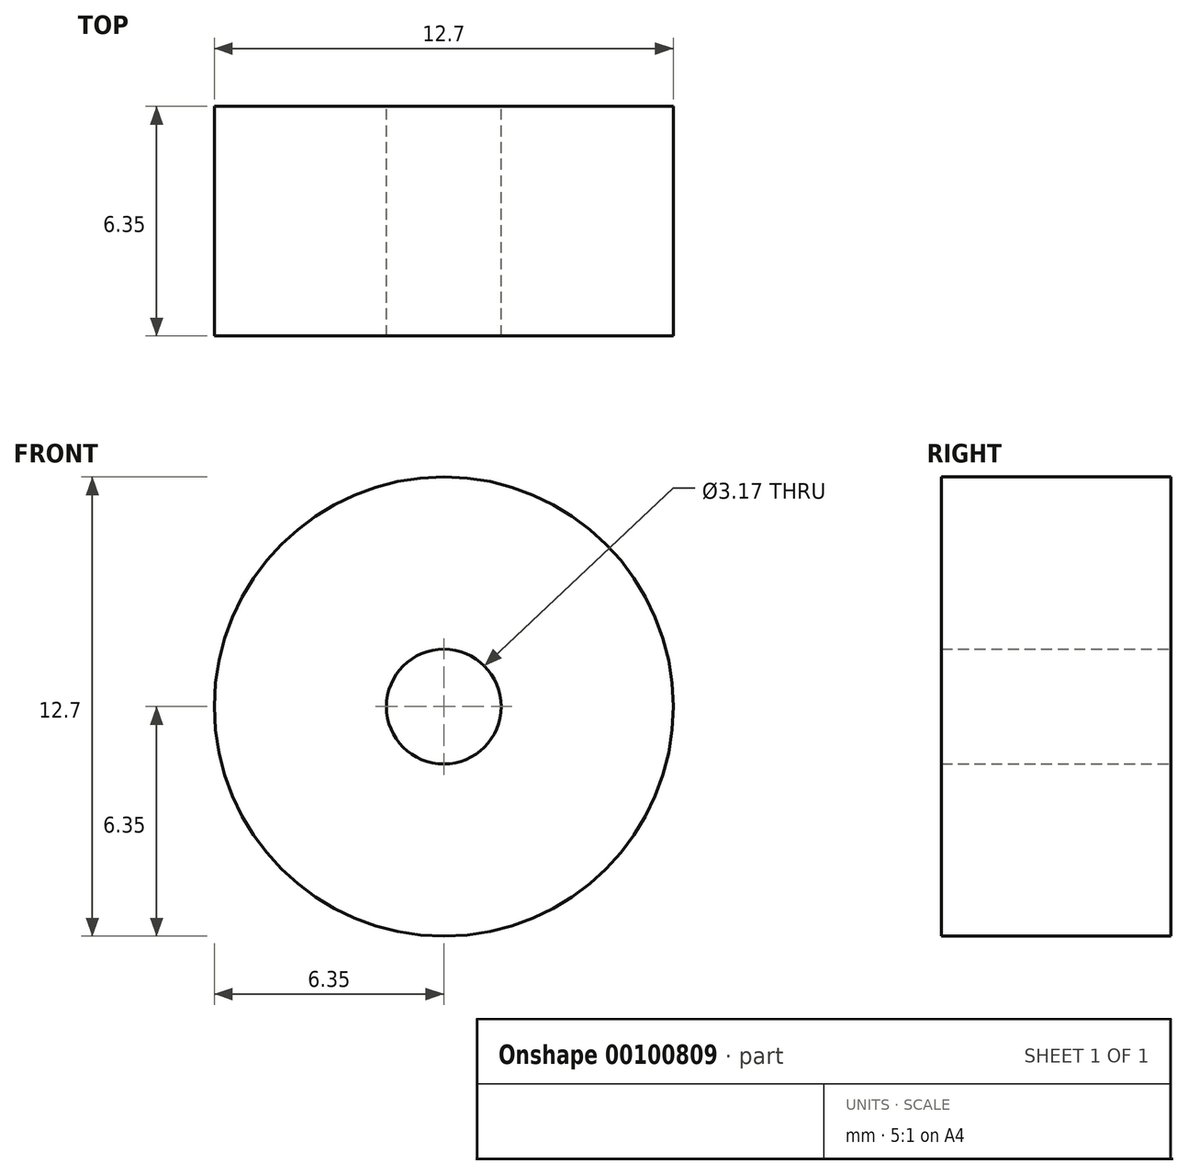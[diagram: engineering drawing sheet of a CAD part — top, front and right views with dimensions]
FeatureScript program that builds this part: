
annotation { "Feature Type Name" : "Feature", "Feature Type Description" : "" }
export const myFeature = defineFeature(function(context is Context, id is Id, definition is map)
    precondition{}
    {
        {
            var Q0;
            Q0=qCreatedBy(makeId("Front.planeOp"),FACE);
            var sketch = newSketch(context, id + "F0", { "sketchPlane" : qUnion([Q0])});
            skCircle(sketch, "E0", {"center": v(0, 0) * mm, "radius": 6.35 * mm});
            skCircle(sketch, "E1", {"center": v(0, 0) * mm, "radius": 1.59 * mm});
            skSolve(sketch);
        }
        {
            var Q0;
            Q0 = qSketchRegion(id + "F0", true);
            extrude(context, id + "F1", {"entities" : qUnion([Q0]), "depth" : 6.35 * mm});
        }
    });
